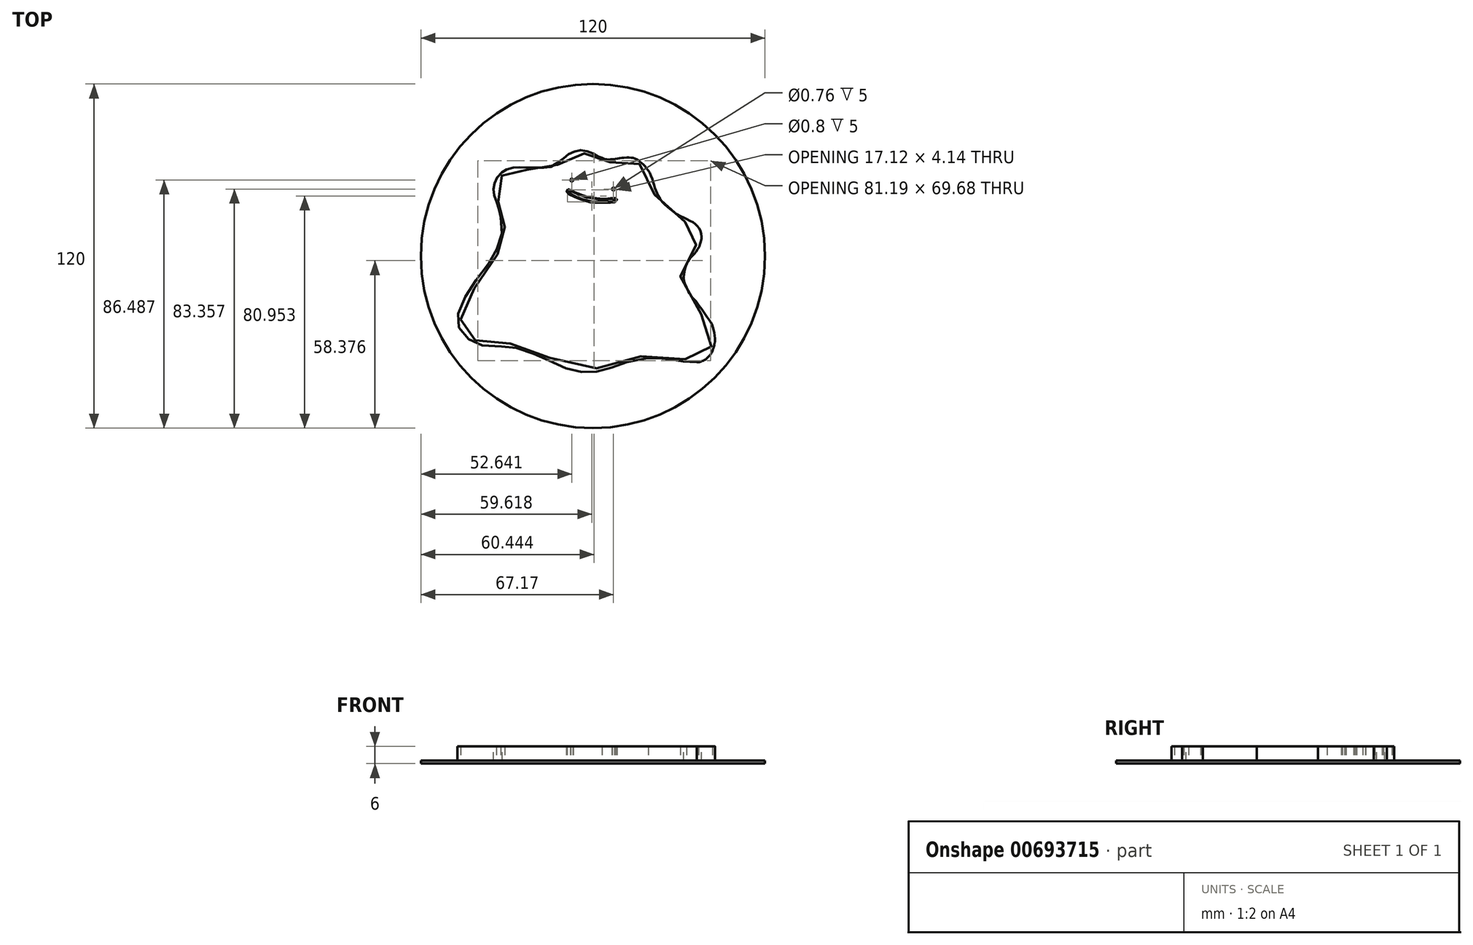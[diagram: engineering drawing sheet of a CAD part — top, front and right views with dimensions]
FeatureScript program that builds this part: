
annotation { "Feature Type Name" : "Feature", "Feature Type Description" : "" }
export const myFeature = defineFeature(function(context is Context, id is Id, definition is map)
    precondition{}
    {
        {
            var Q0;
            Q0=qCreatedBy(makeId("Top.planeOp"),FACE);
            var sketch = newSketch(context, id + "F0", { "sketchPlane" : qUnion([Q0])});
            skFitSpline(sketch, "E0", {"points": [v(0.9, 34.2) * mm, v(2.64, 33.67) * mm, v(4.12, 33.72) * mm, v(6.38, 34) * mm, v(7.91, 34.2) * mm, v(10.18, 34.36) * mm, v(11.59, 34.2) * mm, v(12.73, 33.88) * mm, v(13.96, 33.03) * mm, v(15.36, 31.91) * mm, v(17.02, 29.82) * mm], "startDerivative": vector(17.73, -6.78) * mm, "endDerivative": vector(13.31, -18.7) * mm});
            skFitSpline(sketch, "E1", {"points": [v(17.02, 29.82) * mm, v(17.53, 29) * mm, v(17.99, 27.91) * mm, v(18.47, 26.62) * mm, v(18.8, 25.44) * mm, v(19.19, 24.2) * mm, v(19.53, 23.21) * mm, v(19.82, 22.53) * mm, v(20.22, 21.55) * mm, v(20.76, 20.56) * mm, v(21.67, 19.1) * mm, v(22.7, 17.94) * mm, v(24.69, 16.36) * mm, v(25.69, 15.56) * mm, v(27.05, 14.6) * mm, v(28.54, 13.74) * mm, v(29.94, 13.08) * mm, v(31.32, 12.39) * mm, v(32.65, 11.7) * mm, v(33.4, 11.16) * mm, v(34.1, 10.45) * mm], "startDerivative": vector(12.6, -18.62) * mm, "endDerivative": vector(12.51, -20.85) * mm});
            skFitSpline(sketch, "E2", {"points": [v(34.1, 10.45) * mm, v(34.85, 9.55) * mm, v(35.32, 8.46) * mm, v(35.6, 7.19) * mm, v(35.62, 6.46) * mm, v(35.45, 5.52) * mm, v(35.23, 4.6) * mm, v(34.92, 3.64) * mm, v(34.3, 2.46) * mm, v(33.54, 1.29) * mm, v(32.86, 0.48) * mm, v(31.94, -0.46) * mm, v(31.03, -1.58) * mm, v(30.5, -2.58) * mm, v(30.15, -3.4) * mm, v(29.57, -5.47) * mm, v(29.36, -7.76) * mm, v(29.63, -9.2) * mm, v(29.81, -9.72) * mm, v(30, -10.07) * mm, v(30.34, -10.96) * mm], "startDerivative": vector(16, -17.1) * mm, "endDerivative": vector(8.6, -19.13) * mm});
            skFitSpline(sketch, "E3", {"points": [v(30.34, -10.96) * mm, v(30.62, -11.68) * mm, v(31.15, -12.56) * mm, v(31.54, -13.31) * mm, v(32.32, -14.3) * mm, v(32.9, -14.98) * mm, v(33.82, -16.06) * mm, v(34.47, -16.92) * mm, v(35.38, -18.12) * mm, v(36.17, -19.26) * mm, v(36.86, -20.27) * mm, v(37.71, -21.58) * mm, v(38.75, -22.99) * mm, v(39.28, -24.1) * mm, v(39.72, -25.4) * mm, v(40.06, -26.88) * mm, v(40.23, -28.3) * mm, v(40.28, -29.72) * mm], "startDerivative": vector(4.73, -15.23) * mm, "endDerivative": vector(-1.78, -23.2) * mm});
            skFitSpline(sketch, "E4", {"points": [v(40.28, -29.72) * mm, v(40.05, -30.69) * mm, v(40, -30.87) * mm, v(39.97, -31.13) * mm, v(39.75, -32.15) * mm, v(39.14, -33.57) * mm, v(38.68, -34.34) * mm, v(37.9, -35.24) * mm, v(37.41, -35.74) * mm, v(36.7, -36.25) * mm, v(35.8, -36.63) * mm, v(34.74, -36.95) * mm, v(33.89, -36.95) * mm], "startDerivative": vector(-5.56, -32) * mm, "endDerivative": vector(-9.78, 0.8) * mm});
            skFitSpline(sketch, "E5", {"points": [v(33.89, -36.95) * mm, v(31.51, -36.95) * mm, v(29.47, -36.83) * mm, v(27.24, -36.56) * mm, v(24.77, -36.06) * mm, v(23.39, -35.86) * mm, v(21.91, -35.8) * mm, v(20.38, -35.65) * mm, v(17.74, -35.57) * mm, v(16.71, -35.66) * mm, v(12.8, -36.33) * mm, v(9.13, -37.2) * mm, v(5.96, -38.27) * mm, v(3.47, -39.11) * mm, v(0.92, -39.88) * mm, v(-2.4, -40.49) * mm, v(-4.75, -40.56) * mm, v(-7.63, -40.23) * mm, v(-10.5, -39.47) * mm, v(-13.87, -38.24) * mm, v(-18.16, -36.18) * mm, v(-21.45, -34.75) * mm, v(-24.05, -33.73) * mm, v(-28.51, -32.12) * mm, v(-29.33, -32.05) * mm, v(-31.95, -31.8) * mm, v(-35.93, -31.49) * mm, v(-40.57, -31.23) * mm, v(-42.66, -30.7) * mm, v(-45.32, -29.2) * mm, v(-48.15, -26.46) * mm, v(-49.01, -24.93) * mm, v(-49.42, -22.92) * mm, v(-49.35, -20.5) * mm, v(-47.92, -16.34) * mm, v(-46.29, -13.36) * mm, v(-43.86, -9.6) * mm, v(-40.14, -4.6) * mm, v(-37.95, -1.73) * mm, v(-36.37, 0.92) * mm, v(-35.12, 4.04) * mm, v(-34.2, 7.07) * mm, v(-33.92, 9.95) * mm, v(-34.45, 13.6) * mm], "startDerivative": vector(-115.81, -1.44) * mm, "endDerivative": vector(-28.02, 144.1) * mm});
            skFitSpline(sketch, "E6", {"points": [v(-34.45, 13.6) * mm, v(-35.04, 16.43) * mm, v(-35.86, 18.83) * mm, v(-36.72, 21.3) * mm, v(-36.95, 22.93) * mm, v(-36.77, 24.54) * mm, v(-36.26, 26.32) * mm, v(-35.35, 27.83) * mm, v(-33.64, 29.43) * mm, v(-32.44, 30.17) * mm, v(-30.4, 30.7) * mm, v(-28.7, 30.86) * mm, v(-26.32, 30.89) * mm, v(-23.18, 30.79) * mm, v(-19.74, 30.89) * mm, v(-17.4, 30.94) * mm, v(-15.38, 32) * mm, v(-12.83, 33.82) * mm, v(-11.2, 35.17) * mm, v(-9.64, 36.01) * mm, v(-7.83, 36.8) * mm, v(-6, 36.9) * mm, v(-3.93, 36.47) * mm, v(-2.37, 35.8) * mm, v(-1.1, 35.04) * mm, v(0, 34.48) * mm, v(0.9, 34.2) * mm], "startDerivative": vector(-11.4, 63.85) * mm, "endDerivative": vector(34.08, -8.84) * mm});
            skCircle(sketch, "E7", {"center": v(4.9, 23.36) * mm, "radius": 0.5 * mm});
            skCircle(sketch, "E8", {"center": v(-9.63, 26.49) * mm, "radius": 0.5 * mm});
            skFitSpline(sketch, "E9", {"points": [v(-11.07, 23.32) * mm, v(-10.56, 23.2) * mm, v(-9.95, 22.89) * mm, v(-9.32, 22.58) * mm, v(-8.4, 22.13) * mm, v(-7.73, 21.87) * mm, v(-6.78, 21.52) * mm, v(-5.33, 20.91) * mm, v(-3.64, 20.53) * mm, v(-1.95, 20.22) * mm, v(0, 19.98) * mm, v(1.08, 19.94) * mm, v(2.87, 19.92) * mm, v(4.23, 20.18) * mm, v(5.23, 20.22) * mm, v(5.84, 20.16) * mm, v(6.04, 19.86) * mm, v(6.17, 19.39) * mm, v(5.52, 18.86) * mm, v(4.44, 18.7) * mm, v(3.74, 18.68) * mm, v(3.07, 18.61) * mm, v(1.38, 18.57) * mm, v(-0.24, 18.57) * mm, v(-1.65, 18.6) * mm, v(-3.15, 18.76) * mm, v(-4.25, 19.04) * mm, v(-5.6, 19.39) * mm, v(-6.94, 19.86) * mm, v(-9.16, 20.81) * mm, v(-10.66, 21.6) * mm, v(-11.3, 22.13) * mm, v(-11.48, 22.62) * mm, v(-11.4, 23.11) * mm, v(-11.07, 23.32) * mm]});
            skFitSpline(sketch, "E10", {"points": [v(-35.32, 18.83) * mm, v(-34.4, 16.77) * mm, v(-33.75, 14.57) * mm, v(-33.36, 12.74) * mm, v(-32.97, 10.27) * mm, v(-33.23, 7.4) * mm, v(-33.62, 5.46) * mm, v(-34.14, 3.63) * mm, v(-35.86, 0) * mm, v(-37.92, -3.52) * mm, v(-41.56, -8.33) * mm, v(-45.46, -14.19) * mm, v(-47.02, -16.8) * mm, v(-48.33, -20.56) * mm, v(-48.33, -23.04) * mm, v(-48.06, -24.6) * mm, v(-47.02, -26.16) * mm, v(-44.68, -28.63) * mm, v(-41.95, -29.8) * mm, v(-37.27, -30.45) * mm, v(-33.75, -30.32) * mm, v(-29.33, -30.84) * mm, v(-25.56, -32.01) * mm, v(-19.83, -34.35) * mm, v(-8.38, -39.17) * mm, v(-3.83, -39.56) * mm, v(2.28, -38.52) * mm, v(6.84, -36.7) * mm, v(16.33, -34.75) * mm, v(25.2, -35.12) * mm, v(28.81, -35.82) * mm, v(31.92, -36.22) * mm, v(35.34, -36.02) * mm, v(38.04, -33.73) * mm, v(39.35, -30) * mm, v(39.24, -27.63) * mm, v(37.71, -24.95) * mm, v(34.41, -18.52) * mm, v(30, -13.36) * mm, v(28.25, -7.76) * mm, v(28.8, -4.08) * mm, v(30.72, 0) * mm, v(33.43, 3.57) * mm, v(34.46, 5.72) * mm, v(34.14, 8.67) * mm, v(32.31, 10.9) * mm, v(28.09, 12.65) * mm, v(22.35, 16.64) * mm, v(19.64, 20.54) * mm, v(17.73, 25.56) * mm, v(15.98, 30.1) * mm, v(14.78, 31.38) * mm, v(12.47, 32.97) * mm, v(9.52, 33.3) * mm, v(6.5, 32.97) * mm, v(3.47, 32.73) * mm, v(2.75, 32.73) * mm, v(0.68, 33.21) * mm, v(-1.87, 34.4) * mm, v(-5.38, 35.84) * mm, v(-7.7, 36.16) * mm, v(-9.64, 35.13) * mm, v(-12.23, 33.21) * mm, v(-15.82, 30.98) * mm, v(-17.17, 30.18) * mm, v(-21.45, 30.03) * mm, v(-25.62, 30.1) * mm, v(-29.2, 30.18) * mm, v(-30.64, 29.95) * mm, v(-32.31, 29.47) * mm, v(-33.9, 28.2) * mm, v(-35.26, 26.2) * mm, v(-35.86, 23.1) * mm, v(-35.5, 20.06) * mm, v(-35.32, 18.83) * mm]});
            skCircle(sketch, "E11", {"center": v(4.9, 23.36) * mm, "radius": 0.38 * mm});
            skCircle(sketch, "E12", {"center": v(-9.63, 26.49) * mm, "radius": 0.4 * mm});
            skFitSpline(sketch, "E13", {"points": [v(-11.21, 23.02) * mm, v(-11.26, 22.7) * mm, v(-11.02, 22.26) * mm, v(-10.7, 21.93) * mm, v(-9.16, 21.13) * mm, v(-7, 20.13) * mm, v(-5.6, 19.66) * mm, v(-4.25, 19.39) * mm, v(-3.16, 19.09) * mm, v(-1.74, 18.9) * mm, v(-0.36, 18.8) * mm, v(1.38, 18.85) * mm, v(3, 18.9) * mm, v(3.76, 18.9) * mm, v(4.44, 18.95) * mm, v(5.18, 19.09) * mm, v(5.9, 19.39) * mm, v(5.84, 19.75) * mm, v(5.7, 19.99) * mm, v(5.52, 19.99) * mm, v(4.23, 19.9) * mm, v(2.86, 19.7) * mm, v(1.06, 19.7) * mm, v(0, 19.7) * mm, v(-1.97, 20.04) * mm, v(-3.68, 20.27) * mm, v(-5.33, 20.6) * mm, v(-6.8, 21.27) * mm, v(-7.76, 21.65) * mm, v(-8.4, 21.88) * mm, v(-9.41, 22.36) * mm, v(-9.95, 22.6) * mm, v(-10.6, 22.89) * mm, v(-11.21, 23.02) * mm]});
            skSolve(sketch);
        }
        {
            var Q0;
            Q0=makeQuery(id+"F0.imprint","IMPRINT",FACE,{"disambiguationData":[TD([[makeQuery(id+"F0.imprint","IMPRINT",EDGE,{"derivedFrom":sQuery(id+"F0.wireOp",EDGE,"E0")}),-1.0]])]});
            var Q1;
            Q1=makeQuery(id+"F0.imprint","IMPRINT",FACE,{"disambiguationData":[TD([[makeQuery(id+"F0.imprint","IMPRINT",EDGE,{"derivedFrom":sQuery(id+"F0.wireOp",EDGE,"E9")}),-1.0]])]});
            var Q2;
            Q2=makeQuery(id+"F0.imprint","IMPRINT",FACE,{"disambiguationData":[TD([[makeQuery(id+"F0.imprint","IMPRINT",EDGE,{"derivedFrom":sQuery(id+"F0.wireOp",EDGE,"E8")}),1.0]])]});
            var Q3;
            Q3=makeQuery(id+"F0.imprint","IMPRINT",FACE,{"disambiguationData":[TD([[makeQuery(id+"F0.imprint","IMPRINT",EDGE,{"derivedFrom":sQuery(id+"F0.wireOp",EDGE,"E7")}),1.0]])]});
            extrude(context, id + "F1", {"entities" : qUnion([Q0, Q1, Q2, Q3]), "depth" : 5 * mm, "offsetDistance" : 25 * mm});
        }
        {
            var Q0;
            Q0=qCreatedBy(makeId("Top.planeOp"),FACE);
            var sketch = newSketch(context, id + "F2", { "sketchPlane" : qUnion([Q0])});
            skCircle(sketch, "E14", {"center": v(-2.27, 0) * mm, "radius": 60 * mm});
            skSolve(sketch);
        }
        {
            var Q0;
            Q0 = qSketchRegion(id + "F2", true);
            extrude(context, id + "F3", {"entities" : qUnion([Q0]), "oppositeDirection" : true, "depth" : 1 * mm, "offsetDistance" : 25 * mm});
        }
    });
